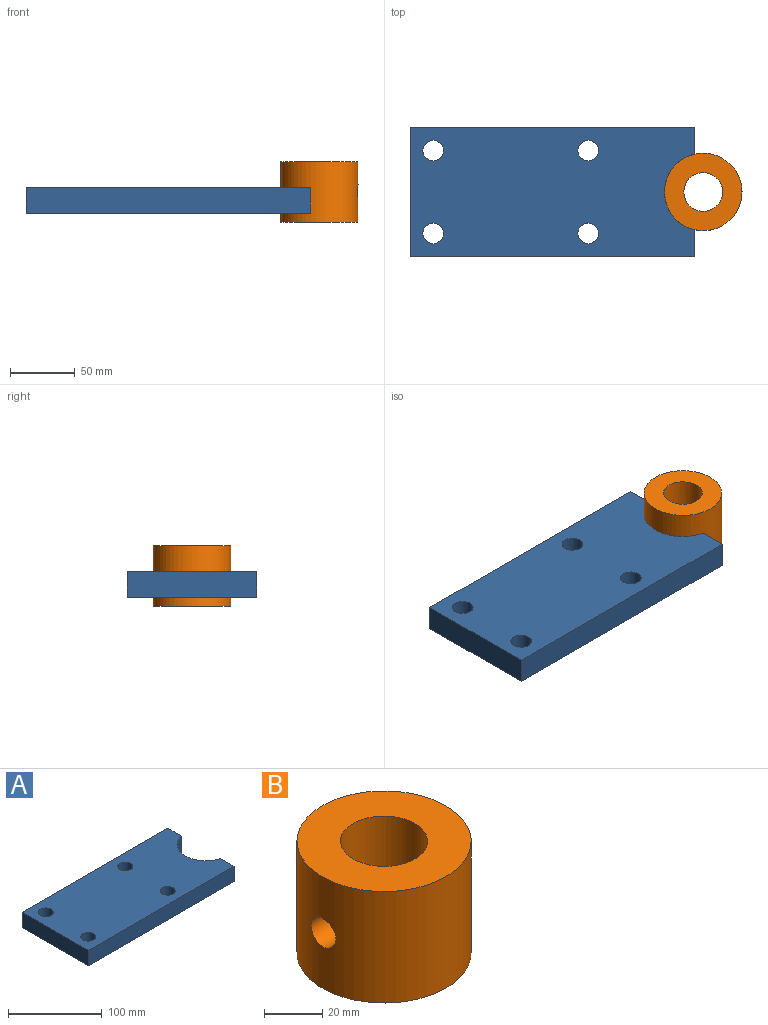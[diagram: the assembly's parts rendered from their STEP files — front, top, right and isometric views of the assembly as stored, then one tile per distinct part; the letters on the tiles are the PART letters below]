
ASSEMBLY  parts=2 mates=1
PART A: 12 faces, bbox 220x100x20 mm
  f0: cylinder r=30mm len=58.34mm, axis (0,0,-1), area 1602.4mm2, adj f1,f5,f10,f11
  f1: plane 20.83x20mm, normal (1,0,0), area 416.6mm2, adj f0,f2,f10,f11
  f2: plane 220x20mm, normal (0,1,0), area 4400mm2, adj f1,f3,f10,f11
  f3: plane 100x20mm, normal (-1,0,0), area 2000mm2, adj f2,f4,f10,f11
  f4: plane 220x20mm, normal (0,-1,0), area 4400mm2, adj f3,f5,f10,f11
  f5: plane 20.83x20mm, normal (1,0,0), area 416.6mm2, adj f0,f4,f10,f11
  f6: cylinder r=8mm len=20mm, axis (0,0,-1), area 1005.3mm2, adj f10,f11
  f7: cylinder r=8mm len=20mm, axis (0,0,-1), area 1005.3mm2, adj f10,f11
  f8: cylinder r=8mm len=20mm, axis (0,0,-1), area 1005.3mm2, adj f10,f11
  f9: cylinder r=8mm len=20mm, axis (0,0,-1), area 1005.3mm2, adj f10,f11
  f10: plane 220x100mm, normal (0,0,1), area 20198.2mm2, adj f0,f1,f2,f3,f4,f5,f6,f7
  f11: plane 220x100mm, normal (0,0,-1), area 20198.2mm2, adj f0,f1,f2,f3,f4,f5,f6,f7
PART B: 5 faces, bbox 60x60x47 mm
  f0: cylinder r=15mm len=47mm, axis (0,0,-1), area 4314.3mm2, adj f2,f3,f4
  f1: cylinder r=30mm len=60mm, axis (0,0,-1), area 8745.1mm2, adj f2,f3,f4
  f2: plane 60x60mm, normal (0,0,1), area 2120.6mm2, adj f0,f1
  f3: plane 60x60mm, normal (0,0,-1), area 2120.6mm2, adj f0,f1
  f4: cylinder r=6mm len=16.25mm, axis (1,0,0), area 577.5mm2, adj f0,f1
PLACE A t=(-42.16,-15.57,13.15)mm
PLACE B rot(axis=(0,0,1),180deg) t=(74.84,-15.57,-3.85)mm
MATE fastened B.f0 <-> A.f0  axis (0,0,-1) through (74.84,-15.57,-3.85)mm
